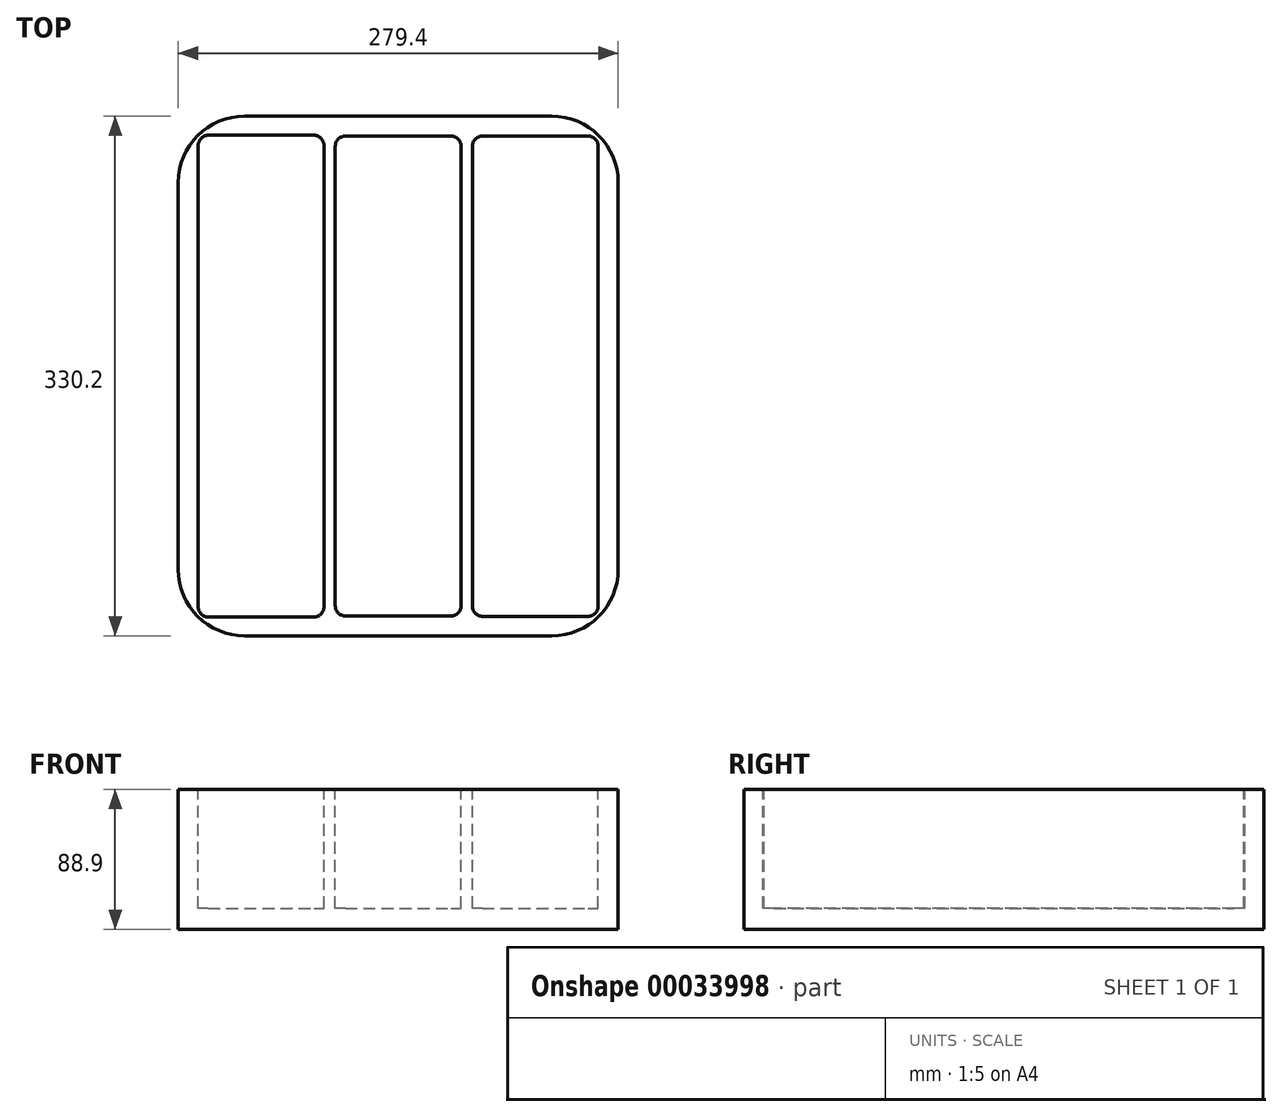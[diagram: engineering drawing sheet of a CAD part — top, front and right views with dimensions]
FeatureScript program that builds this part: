
annotation { "Feature Type Name" : "Feature", "Feature Type Description" : "" }
export const myFeature = defineFeature(function(context is Context, id is Id, definition is map)
    precondition{}
    {
        {
            var Q0;
            Q0=qCreatedBy(makeId("Top.planeOp"),FACE);
            var sketch = newSketch(context, id + "F0", { "sketchPlane" : qUnion([Q0])});
            skLineSegment(sketch, "E0.bottom", {"start": v(0, 0) * mm, "end": v(279.4, 0) * mm});
            skLineSegment(sketch, "E0.top", {"start": v(0, -330.2) * mm, "end": v(279.4, -330.2) * mm});
            skLineSegment(sketch, "E0.left", {"start": v(0, 0) * mm, "end": v(0, -330.2) * mm});
            skLineSegment(sketch, "E0.right", {"start": v(279.4, 0) * mm, "end": v(279.4, -330.2) * mm});
            skSolve(sketch);
        }
        {
            var Q0;
            Q0=makeQuery(id+"F0.imprint","IMPRINT",FACE,{"disambiguationData":[TD([[makeQuery(id+"F0.imprint","IMPRINT",EDGE,{"derivedFrom":sQuery(id+"F0.wireOp",EDGE,"E0.bottom")}),-1.0]])]});
            extrude(context, id + "F1", {"entities" : qUnion([Q0]), "depth" : 88.9 * mm});
        }
        {
            var Q0;
            Q0=makeQuery(id+"F1.opExtrude","SWEPT_EDGE",EDGE,{"disambiguationData":[OSD([sQuery(id+"F0.wireOp",EDGE,"E0.top"),sQuery(id+"F0.wireOp",EDGE,"E0.left")])]});
            var Q1;
            Q1=makeQuery(id+"F1.opExtrude","SWEPT_EDGE",EDGE,{"disambiguationData":[OSD([sQuery(id+"F0.wireOp",EDGE,"E0.top"),sQuery(id+"F0.wireOp",EDGE,"E0.right")])]});
            var Q2;
            Q2=makeQuery(id+"F1.opExtrude","SWEPT_EDGE",EDGE,{"disambiguationData":[OSD([sQuery(id+"F0.wireOp",EDGE,"E0.bottom"),sQuery(id+"F0.wireOp",EDGE,"E0.right")])]});
            var Q3;
            Q3=makeQuery(id+"F1.opExtrude","SWEPT_EDGE",EDGE,{"disambiguationData":[OSD([sQuery(id+"F0.wireOp",EDGE,"E0.bottom"),sQuery(id+"F0.wireOp",EDGE,"E0.left")])]});
            fillet(context, id + "F2", {"entities" : qUnion([Q0, Q1, Q2, Q3]), "radius" : 42.25 * mm, "tangentPropagation" : true, "allowEdgeOverflow" : false});
        }
        {
            var Q0;
            Q0=makeQuery(id+"F1.opExtrude","CAP_FACE",FACE,{"disambiguationData":[OSD([sQuery(id+"F0.wireOp",EDGE,"E0.bottom"),sQuery(id+"F0.wireOp",EDGE,"E0.top"),sQuery(id+"F0.wireOp",EDGE,"E0.left"),sQuery(id+"F0.wireOp",EDGE,"E0.right")])],"isStart":false});
            var sketch = newSketch(context, id + "F3", { "sketchPlane" : qUnion([Q0])});
            skLineSegment(sketch, "E1.bottom", {"start": v(19.05, -12.17) * mm, "end": v(86.2, -12.17) * mm});
            skLineSegment(sketch, "E1.top", {"start": v(19.05, -318.12) * mm, "end": v(86.2, -318.12) * mm});
            skLineSegment(sketch, "E1.left", {"start": v(12.7, -18.52) * mm, "end": v(12.7, -311.77) * mm});
            skLineSegment(sketch, "E1.right", {"start": v(92.56, -18.52) * mm, "end": v(92.56, -311.77) * mm});
            skLineSegment(sketch, "E2.bottom", {"start": v(106.12, -317.5) * mm, "end": v(173.28, -317.5) * mm});
            skLineSegment(sketch, "E2.top", {"start": v(106.12, -12.7) * mm, "end": v(173.28, -12.7) * mm});
            skLineSegment(sketch, "E2.left", {"start": v(99.77, -311.15) * mm, "end": v(99.77, -19.05) * mm});
            skLineSegment(sketch, "E2.right", {"start": v(179.63, -311.15) * mm, "end": v(179.63, -19.05) * mm});
            skLineSegment(sketch, "E3.bottom", {"start": v(193.2, -12.7) * mm, "end": v(260.35, -12.7) * mm});
            skLineSegment(sketch, "E3.top", {"start": v(193.2, -317.74) * mm, "end": v(260.35, -317.74) * mm});
            skLineSegment(sketch, "E3.left", {"start": v(186.84, -19.05) * mm, "end": v(186.84, -311.4) * mm});
            skLineSegment(sketch, "E3.right", {"start": v(266.7, -19.05) * mm, "end": v(266.7, -311.4) * mm});
            skLineSegment(sketch, "E4.0", {"start": v(0, -42.25) * mm, "end": v(0, -287.95) * mm});
            skLineSegment(sketch, "E5.0", {"start": v(279.4, -42.25) * mm, "end": v(279.4, -287.95) * mm});
            skLineSegment(sketch, "E6.0", {"start": v(42.25, 0) * mm, "end": v(237.15, 0) * mm});
            skLineSegment(sketch, "E7.0", {"start": v(42.25, -330.2) * mm, "end": v(237.15, -330.2) * mm});
            skLineSegment(sketch, "E8", {"start": v(139.7, 0) * mm, "end": v(139.7, -277.8) * mm, "construction": true});
            skPoint(sketch, "E9.visualSharp", {"position": v(12.7, -12.17) * mm});
            skArc(sketch, "E9.filletArc", {"start": v(19.05, -12.17) * mm, "mid": v(14.56, -14.03) * mm, "end": v(12.7, -18.52) * mm});
            skPoint(sketch, "E10.visualSharp", {"position": v(92.56, -12.17) * mm});
            skArc(sketch, "E10.filletArc", {"start": v(92.56, -18.52) * mm, "mid": v(90.7, -14.03) * mm, "end": v(86.2, -12.17) * mm});
            skPoint(sketch, "E11.visualSharp", {"position": v(99.77, -12.7) * mm});
            skArc(sketch, "E11.filletArc", {"start": v(106.12, -12.7) * mm, "mid": v(101.63, -14.56) * mm, "end": v(99.77, -19.05) * mm});
            skPoint(sketch, "E12.visualSharp", {"position": v(179.63, -12.7) * mm});
            skArc(sketch, "E12.filletArc", {"start": v(179.63, -19.05) * mm, "mid": v(177.77, -14.56) * mm, "end": v(173.28, -12.7) * mm});
            skPoint(sketch, "E13.visualSharp", {"position": v(266.7, -12.7) * mm});
            skArc(sketch, "E13.filletArc", {"start": v(266.7, -19.05) * mm, "mid": v(264.84, -14.56) * mm, "end": v(260.35, -12.7) * mm});
            skPoint(sketch, "E14.visualSharp", {"position": v(186.84, -317.74) * mm});
            skArc(sketch, "E14.filletArc", {"start": v(186.84, -311.4) * mm, "mid": v(188.7, -315.88) * mm, "end": v(193.2, -317.74) * mm});
            skPoint(sketch, "E15.visualSharp", {"position": v(99.77, -317.5) * mm});
            skArc(sketch, "E15.filletArc", {"start": v(99.77, -311.15) * mm, "mid": v(101.63, -315.64) * mm, "end": v(106.12, -317.5) * mm});
            skPoint(sketch, "E16.visualSharp", {"position": v(12.7, -318.12) * mm});
            skArc(sketch, "E16.filletArc", {"start": v(12.7, -311.77) * mm, "mid": v(14.56, -316.26) * mm, "end": v(19.05, -318.12) * mm});
            skPoint(sketch, "E17.visualSharp", {"position": v(186.84, -12.7) * mm});
            skArc(sketch, "E17.filletArc", {"start": v(193.2, -12.7) * mm, "mid": v(188.7, -14.56) * mm, "end": v(186.84, -19.05) * mm});
            skPoint(sketch, "E18.visualSharp", {"position": v(179.63, -317.5) * mm});
            skArc(sketch, "E18.filletArc", {"start": v(173.28, -317.5) * mm, "mid": v(177.77, -315.64) * mm, "end": v(179.63, -311.15) * mm});
            skPoint(sketch, "E19.visualSharp", {"position": v(92.56, -318.12) * mm});
            skArc(sketch, "E19.filletArc", {"start": v(86.2, -318.12) * mm, "mid": v(90.7, -316.26) * mm, "end": v(92.56, -311.77) * mm});
            skPoint(sketch, "E20.visualSharp", {"position": v(266.7, -317.74) * mm});
            skArc(sketch, "E20.filletArc", {"start": v(260.35, -317.74) * mm, "mid": v(264.84, -315.88) * mm, "end": v(266.7, -311.4) * mm});
            skSolve(sketch);
        }
        {
            var Q0;
            Q0=makeQuery(id+"F3.imprint","IMPRINT",FACE,{"disambiguationData":[TD([[makeQuery(id+"F3.imprint","IMPRINT",EDGE,{"derivedFrom":sQuery(id+"F3.wireOp",EDGE,"E2.bottom")}),1.0]])]});
            var Q1;
            Q1=makeQuery(id+"F3.imprint","IMPRINT",FACE,{"disambiguationData":[TD([[makeQuery(id+"F3.imprint","IMPRINT",EDGE,{"derivedFrom":sQuery(id+"F3.wireOp",EDGE,"E3.bottom")}),-1.0]])]});
            var Q2;
            Q2=makeQuery(id+"F3.imprint","IMPRINT",FACE,{"disambiguationData":[TD([[makeQuery(id+"F3.imprint","IMPRINT",EDGE,{"derivedFrom":sQuery(id+"F3.wireOp",EDGE,"E1.bottom")}),-1.0]])]});
            extrude(context, id + "F4", {"entities" : qUnion([Q0, Q1, Q2]), "operationType" : NewBodyOperationType.REMOVE, "oppositeDirection" : true, "depth" : 75.4 * mm});
        }
    });
